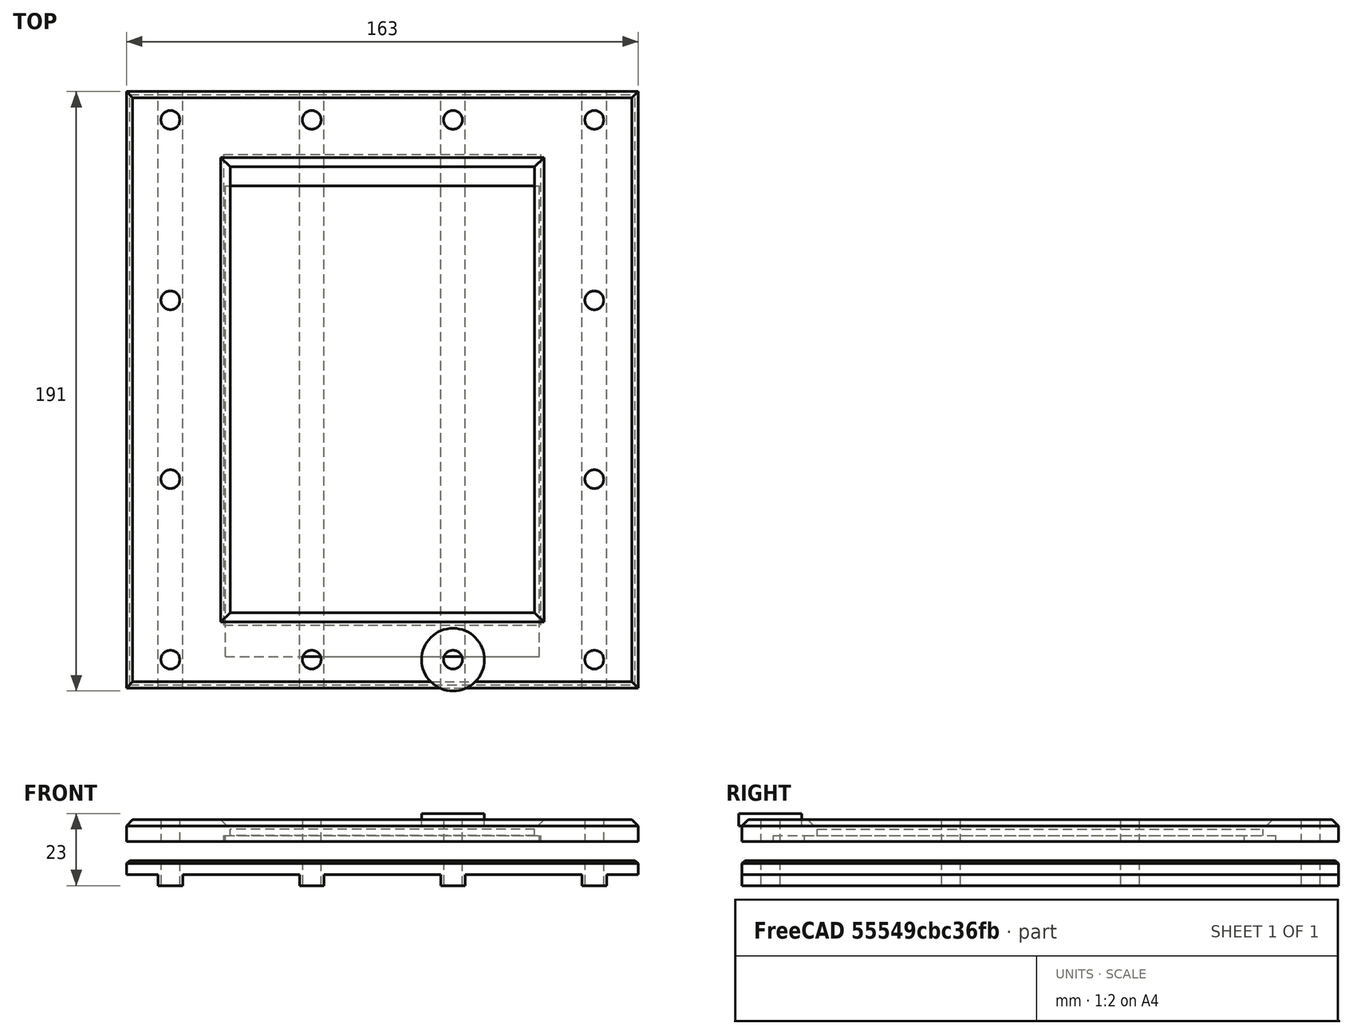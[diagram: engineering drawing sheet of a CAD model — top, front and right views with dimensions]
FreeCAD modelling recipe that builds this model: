
FCSTD DOCUMENT  (FreeCAD 0.20R29410 (Git))
Label: table
License: All rights reserved
LicenseURL: http://en.wikipedia.org/wiki/All_rights_reserved
objects: Part::Cut×31, Part::Cylinder×24, Part::Box×10, Part::Chamfer×3, Part::FeaturePython×1
note: 69 computed .brp shape members not serialized (recipe doc carries the construction recipe); baked Part::Feature solids carry a one-line shape summary decoded from their .brp

FEATURE [Part::Box] Box  label="Cube"
  AttacherType = Attacher::AttachEngine3D
  Height = 8
  Length = 163
  Width = 190
FEATURE [Part::Box] Box001  label="Cube001"
  AttacherType = Attacher::AttachEngine3D
  Height = 3.5
  Length = 37.2
  Placement = pos=(17.9,-5,0) rot=(0,0,1;0rad)
  Width = 200
FEATURE [Part::Box] Box002  label="plate"
  AttacherType = Attacher::AttachEngine3D
  Height = 1.9
  Length = 100
  Placement = pos=(31.5,10,14) rot=(0,0,1;0rad)
  Width = 150
FEATURE [Part::Box] Box003  label="Cube002"
  AttacherType = Attacher::AttachEngine3D
  Height = 3.5
  Length = 37.2
  Placement = pos=(62.9,-5,0) rot=(0,0,1;0rad)
  Width = 200
FEATURE [Part::Box] Box004  label="Cube003"
  AttacherType = Attacher::AttachEngine3D
  Height = 3.5
  Length = 37.2
  Placement = pos=(107.9,-5,0) rot=(0,0,1;0rad)
  Width = 200
FEATURE [Part::Box] Box005  label="Cube004"
  AttacherType = Attacher::AttachEngine3D
  Height = 3.5
  Length = 37.2
  Placement = pos=(152.9,-5,0) rot=(0,0,1;0rad)
  Width = 200
FEATURE [Part::Box] Box006  label="Cube005"
  AttacherType = Attacher::AttachEngine3D
  Height = 3.5
  Length = 37.2
  Placement = pos=(-27.1,-5,0) rot=(0,0,1;0rad)
  Width = 200
FEATURE [Part::Cut] Cut
  Base = -> Box
  Tool = -> Box001
FEATURE [Part::Cut] Cut001
  Base = -> Cut
  Tool = -> Box003
FEATURE [Part::Cut] Cut002
  Base = -> Cut001
  Tool = -> Box004
FEATURE [Part::Cut] Cut003
  Base = -> Cut002
  Tool = -> Box005
FEATURE [Part::Cut] Cut004
  Base = -> Cut003
  Tool = -> Box006
FEATURE [Part::Cylinder] Cylinder
  Angle = 360
  AttacherType = Attacher::AttachEngine3D
  FirstAngle = 0
  Height = 30
  Placement = pos=(14,9,-2) rot=(0,0,1;0rad)
  Radius = 3
  SecondAngle = 0
FEATURE [Part::Cylinder] Cylinder002
  Angle = 360
  AttacherType = Attacher::AttachEngine3D
  FirstAngle = 0
  Height = 30
  Placement = pos=(149,9,-2) rot=(0,0,1;0rad)
  Radius = 3
  SecondAngle = 0
FEATURE [Part::Box] Box009  label="plate002"
  AttacherType = Attacher::AttachEngine3D
  Height = 1.9
  Length = 101
  Placement = pos=(31,20,14) rot=(0,0,1;0rad)
  Width = 150
FEATURE [Part::FeaturePython] Tube  # WARN: FeaturePython — macro-defined, semantics opaque (R4)
  AttacherType = Attacher::AttachEngine3D
  Height = 4
  InnerRadius = 3
  OuterRadius = 10
  Placement = pos=(104,9,19) rot=(0,0,1;0rad)
FEATURE [Part::Box] Box007  label="Cube006"
  AttacherType = Attacher::AttachEngine3D
  Height = 7
  Length = 163
  Placement = pos=(0,0,14) rot=(0,0,1;0rad)
  Width = 190
FEATURE [Part::Box] Box010  label="Cube007"
  AttacherType = Attacher::AttachEngine3D
  Height = 10
  Length = 97
  Placement = pos=(33,24,15) rot=(0,0,1;0rad)
  Width = 142
FEATURE [Part::Cylinder] Cylinder012
  Angle = 360
  AttacherType = Attacher::AttachEngine3D
  FirstAngle = 0
  Height = 30
  Placement = pos=(14,181,-2) rot=(0,0,1;0rad)
  Radius = 3
  SecondAngle = 0
FEATURE [Part::Cylinder] Cylinder013
  Angle = 360
  AttacherType = Attacher::AttachEngine3D
  FirstAngle = 0
  Height = 30
  Placement = pos=(149,181,-2) rot=(0,0,1;0rad)
  Radius = 3
  SecondAngle = 0
FEATURE [Part::Cylinder] Cylinder014
  Angle = 360
  AttacherType = Attacher::AttachEngine3D
  FirstAngle = 0
  Height = 30
  Placement = pos=(14,123.5,-2) rot=(0,0,1;0rad)
  Radius = 3
  SecondAngle = 0
FEATURE [Part::Cylinder] Cylinder015
  Angle = 360
  AttacherType = Attacher::AttachEngine3D
  FirstAngle = 0
  Height = 30
  Placement = pos=(149,123.5,-2) rot=(0,0,1;0rad)
  Radius = 3
  SecondAngle = 0
FEATURE [Part::Cylinder] Cylinder016
  Angle = 360
  AttacherType = Attacher::AttachEngine3D
  FirstAngle = 0
  Height = 30
  Placement = pos=(14,66.5,-2) rot=(0,0,1;0rad)
  Radius = 3
  SecondAngle = 0
FEATURE [Part::Cylinder] Cylinder017
  Angle = 360
  AttacherType = Attacher::AttachEngine3D
  FirstAngle = 0
  Height = 30
  Placement = pos=(149,66.5,-2) rot=(0,0,1;0rad)
  Radius = 3
  SecondAngle = 0
FEATURE [Part::Cylinder] Cylinder018
  Angle = 360
  AttacherType = Attacher::AttachEngine3D
  FirstAngle = 0
  Height = 30
  Placement = pos=(59,181,-2) rot=(0,0,1;0rad)
  Radius = 3
  SecondAngle = 0
FEATURE [Part::Cylinder] Cylinder019
  Angle = 360
  AttacherType = Attacher::AttachEngine3D
  FirstAngle = 0
  Height = 30
  Placement = pos=(104,181,-2) rot=(0,0,1;0rad)
  Radius = 3
  SecondAngle = 0
FEATURE [Part::Cylinder] Cylinder020
  Angle = 360
  AttacherType = Attacher::AttachEngine3D
  FirstAngle = 0
  Height = 30
  Placement = pos=(104,9,-2) rot=(0,0,1;0rad)
  Radius = 3
  SecondAngle = 0
FEATURE [Part::Cylinder] Cylinder021
  Angle = 360
  AttacherType = Attacher::AttachEngine3D
  FirstAngle = 0
  Height = 30
  Placement = pos=(59,9,-2) rot=(0,0,1;0rad)
  Radius = 3
  SecondAngle = 0
FEATURE [Part::Cylinder] Cylinder022
  Angle = 360
  AttacherType = Attacher::AttachEngine3D
  FirstAngle = 0
  Height = 30
  Placement = pos=(14,9,-2) rot=(0,0,1;0rad)
  Radius = 3
  SecondAngle = 0
FEATURE [Part::Cylinder] Cylinder023
  Angle = 360
  AttacherType = Attacher::AttachEngine3D
  FirstAngle = 0
  Height = 30
  Placement = pos=(149,9,-2) rot=(0,0,1;0rad)
  Radius = 3
  SecondAngle = 0
FEATURE [Part::Cylinder] Cylinder024
  Angle = 360
  AttacherType = Attacher::AttachEngine3D
  FirstAngle = 0
  Height = 30
  Placement = pos=(14,181,-2) rot=(0,0,1;0rad)
  Radius = 3
  SecondAngle = 0
FEATURE [Part::Cylinder] Cylinder025
  Angle = 360
  AttacherType = Attacher::AttachEngine3D
  FirstAngle = 0
  Height = 30
  Placement = pos=(149,181,-2) rot=(0,0,1;0rad)
  Radius = 3
  SecondAngle = 0
FEATURE [Part::Cylinder] Cylinder026
  Angle = 360
  AttacherType = Attacher::AttachEngine3D
  FirstAngle = 0
  Height = 30
  Placement = pos=(14,123.5,-2) rot=(0,0,1;0rad)
  Radius = 3
  SecondAngle = 0
FEATURE [Part::Cylinder] Cylinder027
  Angle = 360
  AttacherType = Attacher::AttachEngine3D
  FirstAngle = 0
  Height = 30
  Placement = pos=(149,123.5,-2) rot=(0,0,1;0rad)
  Radius = 3
  SecondAngle = 0
FEATURE [Part::Cylinder] Cylinder028
  Angle = 360
  AttacherType = Attacher::AttachEngine3D
  FirstAngle = 0
  Height = 30
  Placement = pos=(14,66.5,-2) rot=(0,0,1;0rad)
  Radius = 3
  SecondAngle = 0
FEATURE [Part::Cylinder] Cylinder029
  Angle = 360
  AttacherType = Attacher::AttachEngine3D
  FirstAngle = 0
  Height = 30
  Placement = pos=(149,66.5,-2) rot=(0,0,1;0rad)
  Radius = 3
  SecondAngle = 0
FEATURE [Part::Cylinder] Cylinder030
  Angle = 360
  AttacherType = Attacher::AttachEngine3D
  FirstAngle = 0
  Height = 30
  Placement = pos=(59,181,-2) rot=(0,0,1;0rad)
  Radius = 3
  SecondAngle = 0
FEATURE [Part::Cylinder] Cylinder031
  Angle = 360
  AttacherType = Attacher::AttachEngine3D
  FirstAngle = 0
  Height = 30
  Placement = pos=(104,181,-2) rot=(0,0,1;0rad)
  Radius = 3
  SecondAngle = 0
FEATURE [Part::Cylinder] Cylinder032
  Angle = 360
  AttacherType = Attacher::AttachEngine3D
  FirstAngle = 0
  Height = 30
  Placement = pos=(104,9,-2) rot=(0,0,1;0rad)
  Radius = 3
  SecondAngle = 0
FEATURE [Part::Cut] Cut005
  Base = -> Box007
  Tool = -> Cylinder
FEATURE [Part::Cylinder] Cylinder033
  Angle = 360
  AttacherType = Attacher::AttachEngine3D
  FirstAngle = 0
  Height = 30
  Placement = pos=(59,9,-2) rot=(0,0,1;0rad)
  Radius = 3
  SecondAngle = 0
FEATURE [Part::Cut] Cut006
  Base = -> Cut005
  Tool = -> Cylinder021
FEATURE [Part::Cut] Cut007
  Base = -> Cut006
  Tool = -> Cylinder032
FEATURE [Part::Cut] Cut008
  Base = -> Cut007
  Tool = -> Cylinder002
FEATURE [Part::Cut] Cut009
  Base = -> Cut008
  Tool = -> Cylinder017
FEATURE [Part::Cut] Cut010
  Base = -> Cut009
  Tool = -> Cylinder015
FEATURE [Part::Cut] Cut011
  Base = -> Cut010
  Tool = -> Cylinder013
FEATURE [Part::Cut] Cut012
  Base = -> Cut011
  Tool = -> Cylinder019
FEATURE [Part::Cut] Cut013
  Base = -> Cut012
  Tool = -> Cylinder018
FEATURE [Part::Cut] Cut014
  Base = -> Cut013
  Tool = -> Cylinder012
FEATURE [Part::Cut] Cut015
  Base = -> Cut014
  Tool = -> Cylinder014
FEATURE [Part::Cut] Cut016
  Base = -> Cut015
  Tool = -> Cylinder016
FEATURE [Part::Cut] Cut017
  Base = -> Cut004
  Tool = -> Cylinder033
FEATURE [Part::Cut] Cut018
  Base = -> Cut017
  Tool = -> Cylinder022
FEATURE [Part::Cut] Cut019
  Base = -> Cut018
  Tool = -> Cylinder028
FEATURE [Part::Cut] Cut020
  Base = -> Cut019
  Tool = -> Cylinder020
FEATURE [Part::Cut] Cut021
  Base = -> Cut020
  Tool = -> Cylinder023
FEATURE [Part::Cut] Cut022
  Base = -> Cut021
  Tool = -> Cylinder029
FEATURE [Part::Cut] Cut023
  Base = -> Cut022
  Tool = -> Cylinder027
FEATURE [Part::Cut] Cut024
  Base = -> Cut023
  Tool = -> Cylinder026
FEATURE [Part::Cut] Cut025
  Base = -> Cut024
  Tool = -> Cylinder024
FEATURE [Part::Cut] Cut026
  Base = -> Cut025
  Tool = -> Cylinder030
FEATURE [Part::Cut] Cut027
  Base = -> Cut026
  Tool = -> Cylinder031
FEATURE [Part::Cut] Cut028  label="table-bottom"
  Base = -> Cut027
  Tool = -> Cylinder025
FEATURE [Part::Cut] Cut029
  Base = -> Cut016
  Tool = -> Box009
FEATURE [Part::Cut] Cut030
  Base = -> Cut029
  Tool = -> Box010
FEATURE [Part::Chamfer] Chamfer
  Base = -> Cut030
  Edges = 4 edges r=3: [Edge19,Edge20,Edge21,Edge22]
FEATURE [Part::Chamfer] Chamfer001  label="table-top"
  Base = -> Chamfer
  Edges = 4 edges r=2: [Edge5,Edge6,Edge7,Edge8]
FEATURE [Part::Chamfer] Chamfer002  label="table-top001"
  Base = -> Cut028
  Edges = 4 edges r=1: [Edge2,Edge21,Edge24,Edge25]
